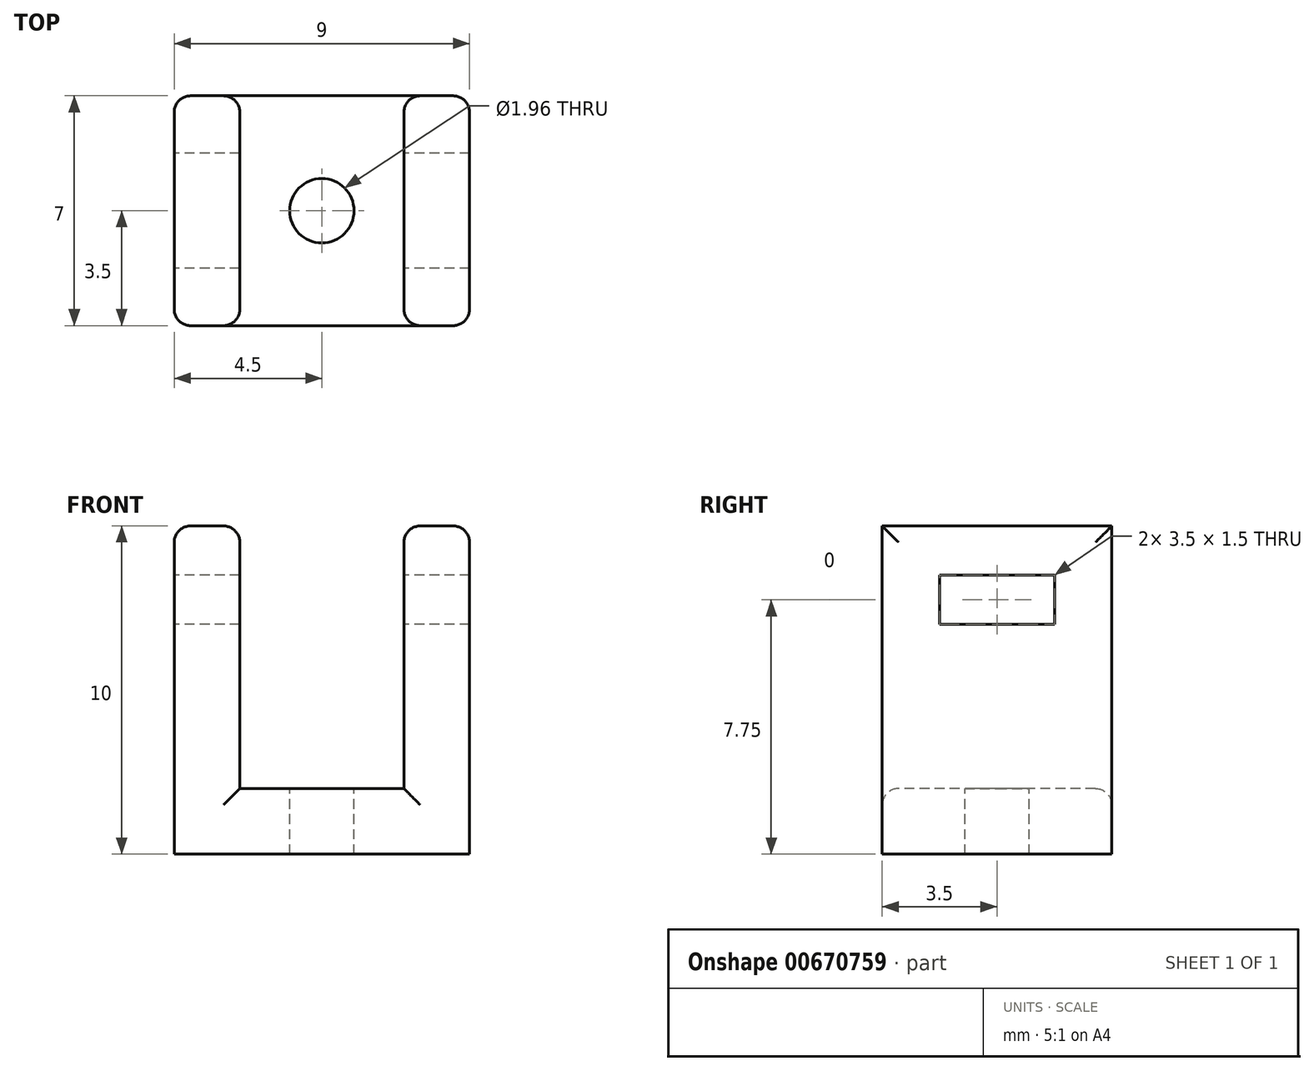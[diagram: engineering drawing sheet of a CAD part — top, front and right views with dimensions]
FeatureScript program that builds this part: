
annotation { "Feature Type Name" : "Feature", "Feature Type Description" : "" }
export const myFeature = defineFeature(function(context is Context, id is Id, definition is map)
    precondition{}
    {
        {
            var Q0;
            Q0=qCreatedBy(makeId("Top.planeOp"),FACE);
            var sketch = newSketch(context, id + "F0", { "sketchPlane" : qUnion([Q0])});
            skLineSegment(sketch, "E0.bottom", {"start": v(4.5, 3.5) * mm, "end": v(-4.5, 3.5) * mm});
            skLineSegment(sketch, "E0.top", {"start": v(4.5, -3.5) * mm, "end": v(-4.5, -3.5) * mm});
            skLineSegment(sketch, "E0.left", {"start": v(4.5, 3.5) * mm, "end": v(4.5, -3.5) * mm});
            skLineSegment(sketch, "E0.right", {"start": v(-4.5, 3.5) * mm, "end": v(-4.5, -3.5) * mm});
            skPoint(sketch, "E0.middle", {"position": v(0, 0) * mm});
            skLineSegment(sketch, "E1", {"start": v(-4.5, 3.5) * mm, "end": v(-2.5, 3.5) * mm, "construction": true});
            skLineSegment(sketch, "E2", {"start": v(-2.5, 3.5) * mm, "end": v(-2.5, -3.5) * mm});
            skLineSegment(sketch, "E3.MirrorCS", {"start": v(2.5, 3.5) * mm, "end": v(2.5, -3.5) * mm});
            skCircle(sketch, "E4", {"center": v(0, 0) * mm, "radius": 0.98 * mm});
            skSolve(sketch);
        }
        {
            var Q0;
            {var subQ0=sQuery(id+"F0.wireOp",EDGE,"E0.right");Q0=makeQuery(id+"F0.imprint","IMPRINT",FACE,{"disambiguationData":[TD([[makeQuery(id+"F0.imprint","IMPRINT",EDGE,{"derivedFrom":subQ0}),1.0]])]});}
            var Q1;
            {var subQ0=sQuery(id+"F0.wireOp",EDGE,"E2");Q1=makeQuery(id+"F0.imprint","IMPRINT",FACE,{"disambiguationData":[TD([[makeQuery(id+"F0.imprint","IMPRINT",EDGE,{"derivedFrom":subQ0}),1.0]])]});}
            var Q2;
            {var subQ0=sQuery(id+"F0.wireOp",EDGE,"E0.left");Q2=makeQuery(id+"F0.imprint","IMPRINT",FACE,{"disambiguationData":[TD([[makeQuery(id+"F0.imprint","IMPRINT",EDGE,{"derivedFrom":subQ0}),-1.0]])]});}
            extrude(context, id + "F1", {"entities" : qUnion([Q0, Q1, Q2]), "oppositeDirection" : true, "depth" : 2 * mm, "offsetDistance" : 25 * mm});
        }
        {
            var Q0;
            {var subQ0=sQuery(id+"F0.wireOp",EDGE,"E0.right");Q0=makeQuery(id+"F0.imprint","IMPRINT",FACE,{"disambiguationData":[TD([[makeQuery(id+"F0.imprint","IMPRINT",EDGE,{"derivedFrom":subQ0}),1.0]])]});}
            var Q1;
            {var subQ0=sQuery(id+"F0.wireOp",EDGE,"E0.left");Q1=makeQuery(id+"F0.imprint","IMPRINT",FACE,{"disambiguationData":[TD([[makeQuery(id+"F0.imprint","IMPRINT",EDGE,{"derivedFrom":subQ0}),-1.0]])]});}
            extrude(context, id + "F2", {"entities" : qUnion([Q0, Q1]), "operationType" : NewBodyOperationType.ADD, "depth" : 8 * mm, "offsetDistance" : 25 * mm});
        }
        {
            var Q0;
            {var subQ0=sQuery(id+"F0.wireOp",EDGE,"E0.right");Q0=makeQuery(id+"F2.boolean.opBoolean","MERGE",FACE,{"derivedFrom":[makeQuery(id+"F1.opExtrude","SWEPT_FACE",FACE,{"disambiguationData":[OSD([subQ0])]}),makeQuery(id+"F2.opExtrude","SWEPT_FACE",FACE,{"disambiguationData":[OSD([subQ0])]})]});}
            var sketch = newSketch(context, id + "F3", { "sketchPlane" : qUnion([Q0])});
            skLineSegment(sketch, "E5.bottom", {"start": v(1.75, 6.5) * mm, "end": v(-1.75, 6.5) * mm});
            skLineSegment(sketch, "E5.top", {"start": v(1.75, 5) * mm, "end": v(-1.75, 5) * mm});
            skLineSegment(sketch, "E5.left", {"start": v(1.75, 6.5) * mm, "end": v(1.75, 5) * mm});
            skLineSegment(sketch, "E5.right", {"start": v(-1.75, 6.5) * mm, "end": v(-1.75, 5) * mm});
            skPoint(sketch, "E5.middle", {"position": v(0, 5.75) * mm});
            skSolve(sketch);
        }
        {
            var Q0;
            Q0 = qSketchRegion(id + "F3", true);
            extrude(context, id + "F4", {"entities" : qUnion([Q0]), "operationType" : NewBodyOperationType.REMOVE, "oppositeDirection" : true, "depth" : 25 * mm, "offsetDistance" : 25 * mm});
        }
        {
            var Q0;
            Q0=makeQuery(id+"F2.opExtrude","SWEPT_EDGE",EDGE,{"disambiguationData":[OSD([sQuery(id+"F0.wireOp",EDGE,"E0.top"),sQuery(id+"F0.wireOp",EDGE,"E2")])]});
            var Q1;
            Q1=makeQuery(id+"F2.opExtrude","CAP_EDGE",EDGE,{"disambiguationData":[OSD([sQuery(id+"F0.wireOp",EDGE,"E0.right")])],"isStart":false});
            var Q2;
            Q2=makeQuery(id+"F2.opExtrude","CAP_EDGE",EDGE,{"disambiguationData":[OSD([sQuery(id+"F0.wireOp",EDGE,"E2")])],"isStart":false});
            var Q3;
            Q3=makeQuery(id+"F2.opExtrude","CAP_EDGE",EDGE,{"disambiguationData":[OSD([sQuery(id+"F0.wireOp",EDGE,"E3.MirrorCS")])],"isStart":false});
            var Q4;
            Q4=makeQuery(id+"F2.opExtrude","CAP_EDGE",EDGE,{"disambiguationData":[OSD([sQuery(id+"F0.wireOp",EDGE,"E0.left")])],"isStart":false});
            var Q5;
            Q5=makeQuery(id+"F2.opExtrude","SWEPT_EDGE",EDGE,{"disambiguationData":[OSD([sQuery(id+"F0.wireOp",EDGE,"E0.top"),sQuery(id+"F0.wireOp",EDGE,"E3.MirrorCS")])]});
            var Q6;
            {var subQ0=sQuery(id+"F0.wireOp",EDGE,"E0.left");var subQ1=sQuery(id+"F0.wireOp",EDGE,"E0.top");Q6=makeQuery(id+"F2.boolean.opBoolean","MERGE",EDGE,{"derivedFrom":[makeQuery(id+"F1.opExtrude","SWEPT_EDGE",EDGE,{"disambiguationData":[OSD([subQ1,subQ0])]}),makeQuery(id+"F2.opExtrude","SWEPT_EDGE",EDGE,{"disambiguationData":[OSD([subQ1,subQ0])]})]});}
            var Q7;
            {var subQ0=sQuery(id+"F0.wireOp",EDGE,"E0.right");var subQ1=sQuery(id+"F0.wireOp",EDGE,"E0.top");Q7=makeQuery(id+"F2.boolean.opBoolean","MERGE",EDGE,{"derivedFrom":[makeQuery(id+"F1.opExtrude","SWEPT_EDGE",EDGE,{"disambiguationData":[OSD([subQ1,subQ0])]}),makeQuery(id+"F2.opExtrude","SWEPT_EDGE",EDGE,{"disambiguationData":[OSD([subQ1,subQ0])]})]});}
            var Q8;
            {var subQ0=sQuery(id+"F0.wireOp",EDGE,"E0.right");var subQ1=sQuery(id+"F0.wireOp",EDGE,"E0.bottom");Q8=makeQuery(id+"F2.boolean.opBoolean","MERGE",EDGE,{"derivedFrom":[makeQuery(id+"F1.opExtrude","SWEPT_EDGE",EDGE,{"disambiguationData":[OSD([subQ1,subQ0])]}),makeQuery(id+"F2.opExtrude","SWEPT_EDGE",EDGE,{"disambiguationData":[OSD([subQ1,subQ0])]})]});}
            var Q9;
            Q9=makeQuery(id+"F2.opExtrude","SWEPT_EDGE",EDGE,{"disambiguationData":[OSD([sQuery(id+"F0.wireOp",EDGE,"E0.bottom"),sQuery(id+"F0.wireOp",EDGE,"E3.MirrorCS")])]});
            var Q10;
            {var subQ0=sQuery(id+"F0.wireOp",EDGE,"E0.left");var subQ1=sQuery(id+"F0.wireOp",EDGE,"E0.bottom");Q10=makeQuery(id+"F2.boolean.opBoolean","MERGE",EDGE,{"derivedFrom":[makeQuery(id+"F1.opExtrude","SWEPT_EDGE",EDGE,{"disambiguationData":[OSD([subQ1,subQ0])]}),makeQuery(id+"F2.opExtrude","SWEPT_EDGE",EDGE,{"disambiguationData":[OSD([subQ1,subQ0])]})]});}
            var Q11;
            Q11=makeQuery(id+"F2.opExtrude","SWEPT_EDGE",EDGE,{"disambiguationData":[OSD([sQuery(id+"F0.wireOp",EDGE,"E0.bottom"),sQuery(id+"F0.wireOp",EDGE,"E2")])]});
            var Q12;
            Q12=makeQuery(id+"F1.opExtrude","CAP_EDGE",EDGE,{"disambiguationData":[OSD([sQuery(id+"F0.wireOp",EDGE,"E0.top")])],"isStart":true});
            var Q13;
            Q13=makeQuery(id+"F1.opExtrude","CAP_EDGE",EDGE,{"disambiguationData":[OSD([sQuery(id+"F0.wireOp",EDGE,"E0.bottom")])],"isStart":true});
            fillet(context, id + "F5", {"entities" : qUnion([Q0, Q1, Q2, Q3, Q4, Q5, Q6, Q7, Q8, Q9, Q10, Q11, Q12, Q13]), "radius" : .5 * mm, "tangentPropagation" : true, "allowEdgeOverflow" : false});
        }
    });
